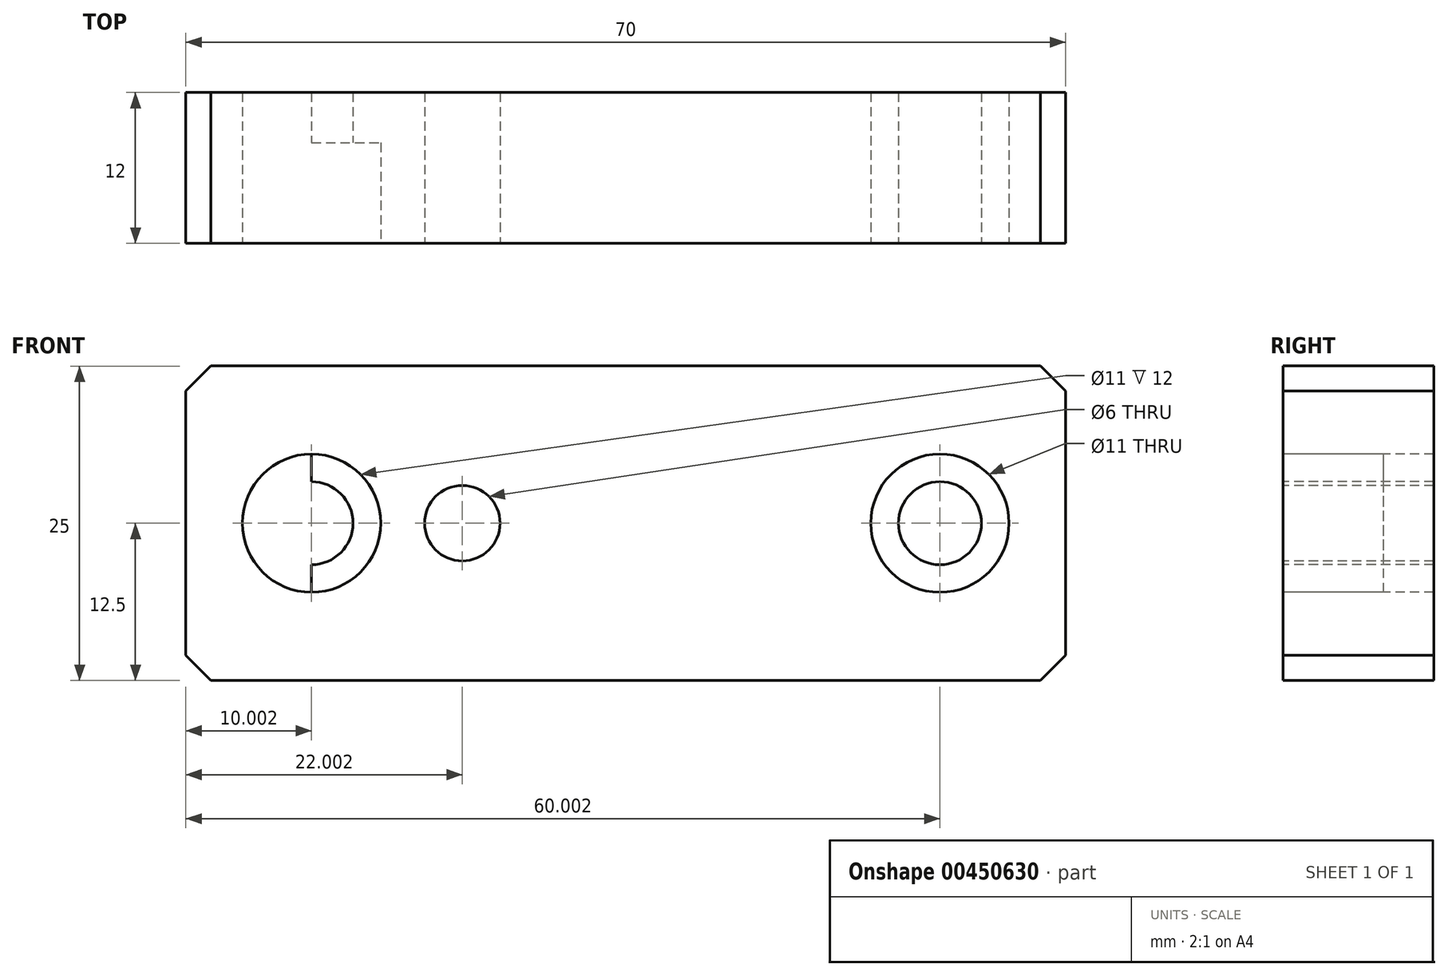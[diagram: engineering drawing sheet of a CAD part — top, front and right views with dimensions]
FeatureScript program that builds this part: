
annotation { "Feature Type Name" : "Feature", "Feature Type Description" : "" }
export const myFeature = defineFeature(function(context is Context, id is Id, definition is map)
    precondition{}
    {
        {
            var Q0;
            Q0=qCreatedBy(makeId("Front.planeOp"),FACE);
            var sketch = newSketch(context, id + "F0", { "sketchPlane" : qUnion([Q0])});
            skLineSegment(sketch, "E0", {"start": v(-114.13, -90.29) * mm, "end": v(-114.13, -111.29) * mm});
            skLineSegment(sketch, "E1", {"start": v(-112.13, -88.29) * mm, "end": v(-114.13, -90.29) * mm});
            skLineSegment(sketch, "E2", {"start": v(-112.13, -113.29) * mm, "end": v(-114.13, -111.29) * mm});
            skLineSegment(sketch, "E3", {"start": v(-46.13, -88.29) * mm, "end": v(-112.13, -88.29) * mm});
            skLineSegment(sketch, "E4", {"start": v(-44.13, -90.29) * mm, "end": v(-46.13, -88.29) * mm});
            skLineSegment(sketch, "E5", {"start": v(-112.13, -113.29) * mm, "end": v(-46.13, -113.29) * mm});
            skLineSegment(sketch, "E6", {"start": v(-44.13, -111.29) * mm, "end": v(-46.13, -113.29) * mm});
            skLineSegment(sketch, "E7", {"start": v(-44.13, -111.29) * mm, "end": v(-44.13, -90.29) * mm});
            skLineSegment(sketch, "E8", {"start": v(40.3, -113.29) * mm, "end": v(40.3, -88.29) * mm});
            skLineSegment(sketch, "E9", {"start": v(40.3, -88.29) * mm, "end": v(28.3, -88.29) * mm});
            skLineSegment(sketch, "E10", {"start": v(40.3, -113.29) * mm, "end": v(28.3, -113.29) * mm});
            skLineSegment(sketch, "E11", {"start": v(28.3, -88.29) * mm, "end": v(28.3, -113.29) * mm});
            skLineSegment(sketch, "E12", {"start": v(24.87, -100.79) * mm, "end": v(42.91, -100.79) * mm});
            skLineSegment(sketch, "E13", {"start": v(-62.38, -100.79) * mm, "end": v(-45.88, -100.79) * mm});
            skCircle(sketch, "E14", {"center": v(-54.13, -100.79) * mm, "radius": 5.5 * mm});
            skLineSegment(sketch, "E15", {"start": v(-54.13, -92.54) * mm, "end": v(-54.13, -109.04) * mm});
            skCircle(sketch, "E16", {"center": v(-54.13, -100.79) * mm, "radius": 3.3 * mm});
            skLineSegment(sketch, "E17", {"start": v(-112.38, -100.79) * mm, "end": v(-95.88, -100.79) * mm});
            skCircle(sketch, "E18", {"center": v(-104.13, -100.79) * mm, "radius": 5.5 * mm});
            skLineSegment(sketch, "E19", {"start": v(-104.13, -92.54) * mm, "end": v(-104.13, -109.04) * mm});
            skCircle(sketch, "E20", {"center": v(-104.13, -100.79) * mm, "radius": 3.3 * mm});
            skLineSegment(sketch, "E21", {"start": v(-87.63, -100.79) * mm, "end": v(-96.63, -100.79) * mm});
            skCircle(sketch, "E22", {"center": v(-92.13, -100.79) * mm, "radius": 3 * mm});
            skLineSegment(sketch, "E23", {"start": v(-92.13, -105.29) * mm, "end": v(-92.13, -96.29) * mm});
            skCircle(sketch, "E24", {"center": v(-92.13, -100.79) * mm, "radius": 2.46 * mm});
            skSolve(sketch);
        }
        {
            var Q0;
            {var subQ0=sQuery(id+"F0.wireOp",EDGE,"E18");var subQ1=sQuery(id+"F0.wireOp",EDGE,"E17");var subQ2=makeQuery(id+"F0.imprint","INTERSECT",VERTEX,{"disambiguationData":[OD(1.0)],"derivedFrom":[subQ1,subQ0]});Q0=makeQuery(id+"F0.imprint","IMPRINT",FACE,{"disambiguationData":[TD([[makeQuery(id+"F0.imprint","IMPRINT",EDGE,{"disambiguationData":[TD([[subQ2,1.0]])],"derivedFrom":subQ1}),1.0]])]});}
            var Q1;
            {var subQ0=sQuery(id+"F0.wireOp",EDGE,"E18");var subQ1=sQuery(id+"F0.wireOp",EDGE,"E17");var subQ2=makeQuery(id+"F0.imprint","INTERSECT",VERTEX,{"disambiguationData":[OD(0.0)],"derivedFrom":[subQ1,subQ0]});Q1=makeQuery(id+"F0.imprint","IMPRINT",FACE,{"disambiguationData":[TD([[makeQuery(id+"F0.imprint","IMPRINT",EDGE,{"disambiguationData":[TD([[subQ2,-1.0]])],"derivedFrom":subQ1}),1.0]])]});}
            var Q2;
            {var subQ0=sQuery(id+"F0.wireOp",EDGE,"E14");var subQ1=sQuery(id+"F0.wireOp",EDGE,"E13");var subQ2=makeQuery(id+"F0.imprint","INTERSECT",VERTEX,{"disambiguationData":[OD(1.0)],"derivedFrom":[subQ1,subQ0]});Q2=makeQuery(id+"F0.imprint","IMPRINT",FACE,{"disambiguationData":[TD([[makeQuery(id+"F0.imprint","IMPRINT",EDGE,{"disambiguationData":[TD([[subQ2,1.0]])],"derivedFrom":subQ1}),1.0]])]});}
            var Q3;
            Q3=makeQuery(id+"F0.imprint","IMPRINT",FACE,{"disambiguationData":[TD([[makeQuery(id+"F0.imprint","IMPRINT",EDGE,{"derivedFrom":sQuery(id+"F0.wireOp",EDGE,"E0")}),1.0]])]});
            var Q4;
            {var subQ0=sQuery(id+"F0.wireOp",EDGE,"E18");var subQ1=sQuery(id+"F0.wireOp",EDGE,"E17");var subQ2=makeQuery(id+"F0.imprint","INTERSECT",VERTEX,{"disambiguationData":[OD(1.0)],"derivedFrom":[subQ1,subQ0]});Q4=makeQuery(id+"F0.imprint","IMPRINT",FACE,{"disambiguationData":[TD([[makeQuery(id+"F0.imprint","IMPRINT",EDGE,{"disambiguationData":[TD([[subQ2,1.0]])],"derivedFrom":subQ1}),-1.0]])]});}
            var Q5;
            {var subQ0=sQuery(id+"F0.wireOp",EDGE,"E14");var subQ1=sQuery(id+"F0.wireOp",EDGE,"E13");var subQ2=makeQuery(id+"F0.imprint","INTERSECT",VERTEX,{"disambiguationData":[OD(0.0)],"derivedFrom":[subQ1,subQ0]});Q5=makeQuery(id+"F0.imprint","IMPRINT",FACE,{"disambiguationData":[TD([[makeQuery(id+"F0.imprint","IMPRINT",EDGE,{"disambiguationData":[TD([[subQ2,-1.0]])],"derivedFrom":subQ1}),1.0]])]});}
            var Q6;
            {var subQ0=sQuery(id+"F0.wireOp",EDGE,"E18");var subQ1=sQuery(id+"F0.wireOp",EDGE,"E17");var subQ2=makeQuery(id+"F0.imprint","INTERSECT",VERTEX,{"disambiguationData":[OD(0.0)],"derivedFrom":[subQ1,subQ0]});Q6=makeQuery(id+"F0.imprint","IMPRINT",FACE,{"disambiguationData":[TD([[makeQuery(id+"F0.imprint","IMPRINT",EDGE,{"disambiguationData":[TD([[subQ2,-1.0]])],"derivedFrom":subQ1}),-1.0]])]});}
            var Q7;
            {var subQ0=sQuery(id+"F0.wireOp",EDGE,"E14");var subQ1=sQuery(id+"F0.wireOp",EDGE,"E13");var subQ2=makeQuery(id+"F0.imprint","INTERSECT",VERTEX,{"disambiguationData":[OD(1.0)],"derivedFrom":[subQ1,subQ0]});Q7=makeQuery(id+"F0.imprint","IMPRINT",FACE,{"disambiguationData":[TD([[makeQuery(id+"F0.imprint","IMPRINT",EDGE,{"disambiguationData":[TD([[subQ2,1.0]])],"derivedFrom":subQ1}),-1.0]])]});}
            var Q8;
            {var subQ0=sQuery(id+"F0.wireOp",EDGE,"E14");var subQ1=sQuery(id+"F0.wireOp",EDGE,"E13");var subQ2=makeQuery(id+"F0.imprint","INTERSECT",VERTEX,{"disambiguationData":[OD(0.0)],"derivedFrom":[subQ1,subQ0]});Q8=makeQuery(id+"F0.imprint","IMPRINT",FACE,{"disambiguationData":[TD([[makeQuery(id+"F0.imprint","IMPRINT",EDGE,{"disambiguationData":[TD([[subQ2,-1.0]])],"derivedFrom":subQ1}),-1.0]])]});}
            var Q9;
            {var subQ0=sQuery(id+"F0.wireOp",EDGE,"E16");var subQ1=sQuery(id+"F0.wireOp",EDGE,"E13");var subQ2=makeQuery(id+"F0.imprint","INTERSECT",VERTEX,{"disambiguationData":[OD(0.0)],"derivedFrom":[subQ1,subQ0]});Q9=makeQuery(id+"F0.imprint","IMPRINT",FACE,{"disambiguationData":[TD([[makeQuery(id+"F0.imprint","IMPRINT",EDGE,{"disambiguationData":[TD([[subQ2,-1.0]])],"derivedFrom":subQ1}),1.0]])]});}
            var Q10;
            {var subQ0=sQuery(id+"F0.wireOp",EDGE,"E16");var subQ1=sQuery(id+"F0.wireOp",EDGE,"E13");var subQ2=makeQuery(id+"F0.imprint","INTERSECT",VERTEX,{"disambiguationData":[OD(0.0)],"derivedFrom":[subQ1,subQ0]});Q10=makeQuery(id+"F0.imprint","IMPRINT",FACE,{"disambiguationData":[TD([[makeQuery(id+"F0.imprint","IMPRINT",EDGE,{"disambiguationData":[TD([[subQ2,-1.0]])],"derivedFrom":subQ1}),-1.0]])]});}
            var Q11;
            {var subQ0=sQuery(id+"F0.wireOp",EDGE,"E15");var subQ1=sQuery(id+"F0.wireOp",EDGE,"E13");var subQ2=makeQuery(id+"F0.imprint","INTERSECT",VERTEX,{"derivedFrom":[subQ1,subQ0]});Q11=makeQuery(id+"F0.imprint","IMPRINT",FACE,{"disambiguationData":[TD([[makeQuery(id+"F0.imprint","IMPRINT",EDGE,{"disambiguationData":[TD([[subQ2,-1.0]])],"derivedFrom":subQ1}),1.0]])]});}
            var Q12;
            {var subQ0=sQuery(id+"F0.wireOp",EDGE,"E15");var subQ1=sQuery(id+"F0.wireOp",EDGE,"E13");var subQ2=makeQuery(id+"F0.imprint","INTERSECT",VERTEX,{"derivedFrom":[subQ1,subQ0]});Q12=makeQuery(id+"F0.imprint","IMPRINT",FACE,{"disambiguationData":[TD([[makeQuery(id+"F0.imprint","IMPRINT",EDGE,{"disambiguationData":[TD([[subQ2,-1.0]])],"derivedFrom":subQ1}),-1.0]])]});}
            var Q13;
            {var subQ0=sQuery(id+"F0.wireOp",EDGE,"E20");var subQ1=sQuery(id+"F0.wireOp",EDGE,"E17");var subQ2=makeQuery(id+"F0.imprint","INTERSECT",VERTEX,{"disambiguationData":[OD(0.0)],"derivedFrom":[subQ1,subQ0]});Q13=makeQuery(id+"F0.imprint","IMPRINT",FACE,{"disambiguationData":[TD([[makeQuery(id+"F0.imprint","IMPRINT",EDGE,{"disambiguationData":[TD([[subQ2,-1.0]])],"derivedFrom":subQ1}),1.0]])]});}
            var Q14;
            {var subQ0=sQuery(id+"F0.wireOp",EDGE,"E20");var subQ1=sQuery(id+"F0.wireOp",EDGE,"E17");var subQ2=makeQuery(id+"F0.imprint","INTERSECT",VERTEX,{"disambiguationData":[OD(0.0)],"derivedFrom":[subQ1,subQ0]});Q14=makeQuery(id+"F0.imprint","IMPRINT",FACE,{"disambiguationData":[TD([[makeQuery(id+"F0.imprint","IMPRINT",EDGE,{"disambiguationData":[TD([[subQ2,-1.0]])],"derivedFrom":subQ1}),-1.0]])]});}
            var Q15;
            {var subQ0=sQuery(id+"F0.wireOp",EDGE,"E19");var subQ1=sQuery(id+"F0.wireOp",EDGE,"E17");var subQ2=makeQuery(id+"F0.imprint","INTERSECT",VERTEX,{"derivedFrom":[subQ1,subQ0]});Q15=makeQuery(id+"F0.imprint","IMPRINT",FACE,{"disambiguationData":[TD([[makeQuery(id+"F0.imprint","IMPRINT",EDGE,{"disambiguationData":[TD([[subQ2,-1.0]])],"derivedFrom":subQ1}),1.0]])]});}
            var Q16;
            {var subQ0=sQuery(id+"F0.wireOp",EDGE,"E19");var subQ1=sQuery(id+"F0.wireOp",EDGE,"E17");var subQ2=makeQuery(id+"F0.imprint","INTERSECT",VERTEX,{"derivedFrom":[subQ1,subQ0]});Q16=makeQuery(id+"F0.imprint","IMPRINT",FACE,{"disambiguationData":[TD([[makeQuery(id+"F0.imprint","IMPRINT",EDGE,{"disambiguationData":[TD([[subQ2,-1.0]])],"derivedFrom":subQ1}),-1.0]])]});}
            extrude(context, id + "F1", {"entities" : qUnion([Q0, Q1, Q2, Q3, Q4, Q5, Q6, Q7, Q8, Q9, Q10, Q11, Q12, Q13, Q14, Q15, Q16]), "oppositeDirection" : true, "depth" : 12 * mm});
        }
        {
            var Q0;
            Q0=sQuery(id+"F0.wireOp",VERTEX,"E16.center");
            var Q1;
            Q1=sQuery(id+"F0.wireOp",VERTEX,"E20.center");
            var Q2;
            Q2=makeQuery(id+"F1.opExtrude","SWEPT_BODY",BODY,{"disambiguationData":[OSD([sQuery(id+"F0.wireOp",EDGE,"E0"),sQuery(id+"F0.wireOp",EDGE,"E1"),sQuery(id+"F0.wireOp",EDGE,"E2"),sQuery(id+"F0.wireOp",EDGE,"E3"),sQuery(id+"F0.wireOp",EDGE,"E4"),sQuery(id+"F0.wireOp",EDGE,"E5"),sQuery(id+"F0.wireOp",EDGE,"E6"),sQuery(id+"F0.wireOp",EDGE,"E7"),sQuery(id+"F0.wireOp",EDGE,"E22")])]});
            hole(context, id + "F2", {"style" : HoleStyle.C_BORE, "endStyle" : HoleEndStyle.THROUGH, "holeDiameter" : 6.6 * mm, "cBoreDiameter" : 11 * mm, "cBoreDepth" : 8 * mm, "isTappedThrough" : true, "tappedDepth" : 12 * mm, "tapClearance" : 3, "locations" : qUnion([Q0, Q1]), "scope" : qUnion([Q2])});
        }
    });
